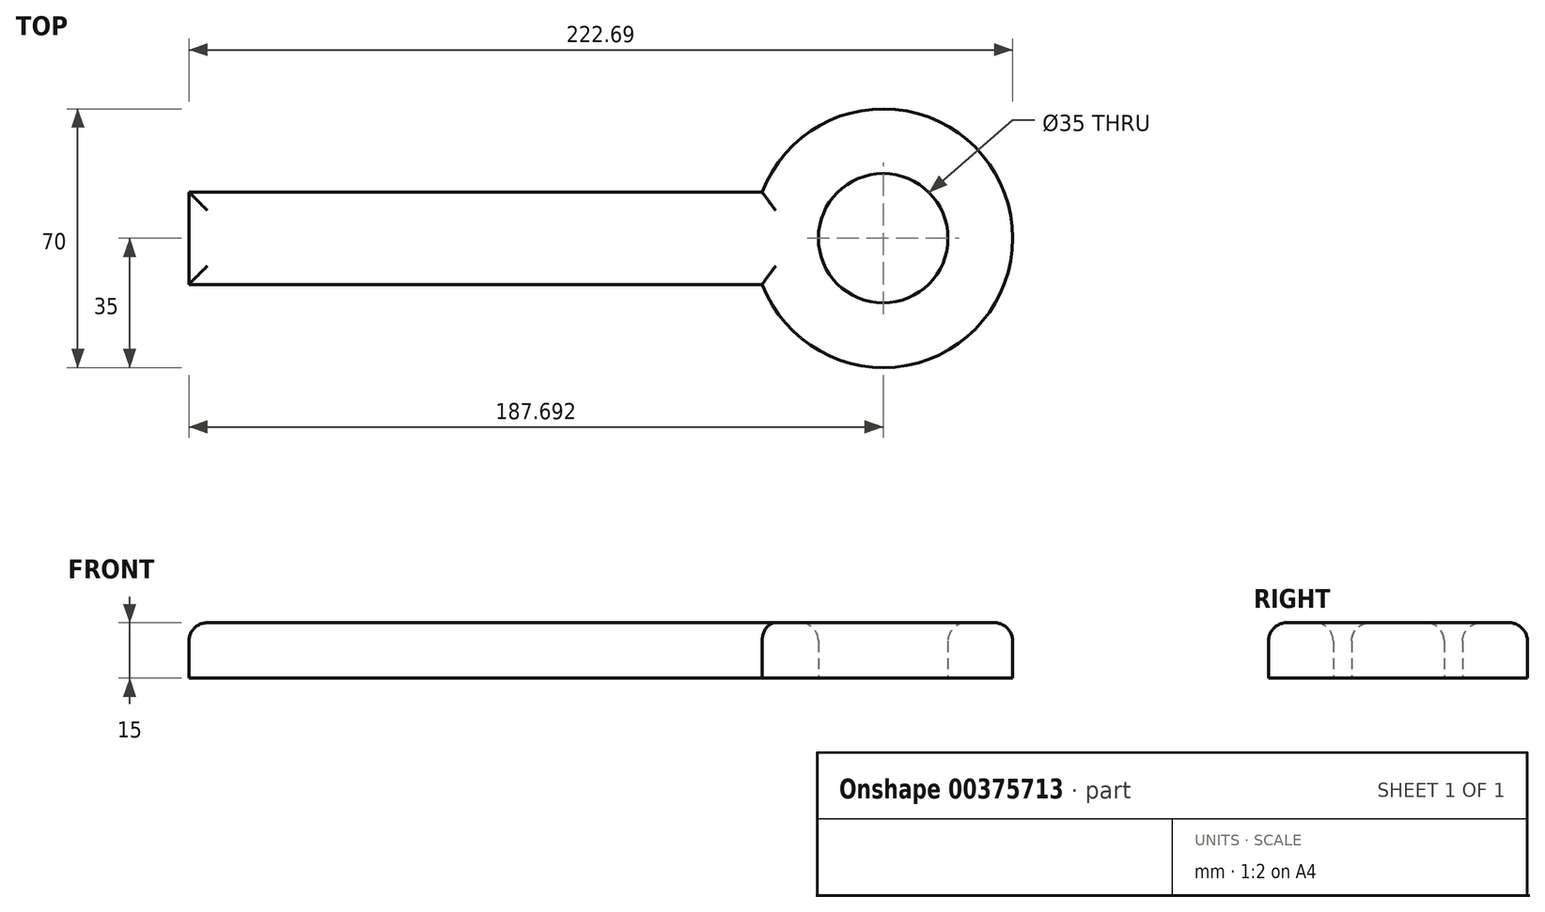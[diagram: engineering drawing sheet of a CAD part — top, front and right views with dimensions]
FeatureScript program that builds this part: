
annotation { "Feature Type Name" : "Feature", "Feature Type Description" : "" }
export const myFeature = defineFeature(function(context is Context, id is Id, definition is map)
    precondition{}
    {
        {
            var Q0;
            Q0=qCreatedBy(makeId("Top.planeOp"),FACE);
            var sketch = newSketch(context, id + "F0", { "sketchPlane" : qUnion([Q0])});
            skLineSegment(sketch, "E0.bottom", {"start": v(0, 0) * mm, "end": v(-155, 0) * mm});
            skLineSegment(sketch, "E0.top", {"start": v(0, 25) * mm, "end": v(-155, 25) * mm});
            skLineSegment(sketch, "E0.left", {"start": v(0, 0) * mm, "end": v(0, 25) * mm});
            skLineSegment(sketch, "E0.right", {"start": v(-155, 0) * mm, "end": v(-155, 25) * mm});
            skLineSegment(sketch, "E1.bottom", {"start": v(-155, 0) * mm, "end": v(-145, 0) * mm});
            skLineSegment(sketch, "E1.top", {"start": v(-155, -30) * mm, "end": v(-145, -30) * mm});
            skLineSegment(sketch, "E1.left", {"start": v(-155, 0) * mm, "end": v(-155, -30) * mm});
            skLineSegment(sketch, "E1.right", {"start": v(-145, 0) * mm, "end": v(-145, -30) * mm});
            skLineSegment(sketch, "E2.bottom", {"start": v(-130.68, 0) * mm, "end": v(-122.68, 0) * mm});
            skLineSegment(sketch, "E2.top", {"start": v(-130.68, -15) * mm, "end": v(-122.68, -15) * mm});
            skLineSegment(sketch, "E2.left", {"start": v(-130.68, 0) * mm, "end": v(-130.68, -15) * mm});
            skLineSegment(sketch, "E2.right", {"start": v(-122.68, 0) * mm, "end": v(-122.68, -15) * mm});
            skLineSegment(sketch, "E3", {"start": v(-94.28, 0) * mm, "end": v(-108.28, 0) * mm});
            skLineSegment(sketch, "E4", {"start": v(-94.28, 0) * mm, "end": v(-101.28, -15) * mm});
            skLineSegment(sketch, "E5", {"start": v(-108.28, 0) * mm, "end": v(-101.28, -15) * mm});
            skArc(sketch, "E6", {"start": v(0, 0) * mm, "mid": v(67.7, 12.5) * mm, "end": v(0, 25) * mm});
            skCircle(sketch, "E7", {"center": v(32.7, 12.5) * mm, "radius": 17.5 * mm});
            skLineSegment(sketch, "E8", {"start": v(32.7, 12.5) * mm, "end": v(-155, 12.5) * mm, "construction": true});
            skLineSegment(sketch, "E9", {"start": v(-101.28, -15) * mm, "end": v(-101.28, 0) * mm, "construction": true});
            skSolve(sketch);
        }
        {
            var Q0;
            Q0=makeQuery(id+"F0.imprint","IMPRINT",FACE,{"disambiguationData":[TD([[makeQuery(id+"F0.imprint","IMPRINT",EDGE,{"derivedFrom":sQuery(id+"F0.wireOp",EDGE,"E0.top")}),1.0]])]});
            var Q1;
            Q1=makeQuery(id+"F0.imprint","IMPRINT",FACE,{"disambiguationData":[TD([[makeQuery(id+"F0.imprint","IMPRINT",EDGE,{"derivedFrom":sQuery(id+"F0.wireOp",EDGE,"E0.left")}),-1.0]])]});
            var Q2;
            Q2=makeQuery(id+"F0.imprint","IMPRINT",FACE,{"disambiguationData":[TD([[makeQuery(id+"F0.imprint","IMPRINT",EDGE,{"derivedFrom":sQuery(id+"F0.wireOp",EDGE,"E1.bottom")}),-1.0]])]});
            var Q3;
            Q3=makeQuery(id+"F0.imprint","IMPRINT",FACE,{"disambiguationData":[TD([[makeQuery(id+"F0.imprint","IMPRINT",EDGE,{"derivedFrom":sQuery(id+"F0.wireOp",EDGE,"E2.bottom")}),-1.0]])]});
            var Q4;
            Q4=makeQuery(id+"F0.imprint","IMPRINT",FACE,{"disambiguationData":[TD([[makeQuery(id+"F0.imprint","IMPRINT",EDGE,{"derivedFrom":sQuery(id+"F0.wireOp",EDGE,"E3")}),1.0]])]});
            extrude(context, id + "F1", {"entities" : qUnion([Q0, Q1, Q2, Q3, Q4]), "depth" : 15 * mm});
        }
        {
            var Q0;
            Q0=makeQuery(id+"F1.opExtrude","CAP_EDGE",EDGE,{"disambiguationData":[OSD([sQuery(id+"F0.wireOp",EDGE,"E0.top")])],"isStart":false});
            var Q1;
            Q1=makeQuery(id+"F1.opExtrude","CAP_EDGE",EDGE,{"disambiguationData":[OSD([sQuery(id+"F0.wireOp",EDGE,"E0.right"),sQuery(id+"F0.wireOp",EDGE,"E1.left")])],"isStart":false});
            var Q2;
            Q2=makeQuery(id+"F1.opExtrude","CAP_FACE",FACE,{"disambiguationData":[OSD([sQuery(id+"F0.wireOp",EDGE,"E0.bottom"),sQuery(id+"F0.wireOp",EDGE,"E0.top"),sQuery(id+"F0.wireOp",EDGE,"E0.right"),sQuery(id+"F0.wireOp",EDGE,"E1.top"),sQuery(id+"F0.wireOp",EDGE,"E1.left"),sQuery(id+"F0.wireOp",EDGE,"E1.right"),sQuery(id+"F0.wireOp",EDGE,"E2.top"),sQuery(id+"F0.wireOp",EDGE,"E2.left"),sQuery(id+"F0.wireOp",EDGE,"E2.right"),sQuery(id+"F0.wireOp",EDGE,"E4"),sQuery(id+"F0.wireOp",EDGE,"E5"),sQuery(id+"F0.wireOp",EDGE,"E6"),sQuery(id+"F0.wireOp",EDGE,"E7")])],"isStart":false});
            var Q3;
            Q3=makeQuery(id+"F1.opExtrude","CAP_EDGE",EDGE,{"disambiguationData":[OSD([sQuery(id+"F0.wireOp",EDGE,"E1.right")])],"isStart":false});
            var Q4;
            Q4=makeQuery(id+"F1.opExtrude","CAP_EDGE",EDGE,{"disambiguationData":[OSD([sQuery(id+"F0.wireOp",EDGE,"E2.left")])],"isStart":false});
            var Q5;
            {var subQ0=sQuery(id+"F0.wireOp",EDGE,"E0.bottom");Q5=makeQuery(id+"F1.opExtrude","CAP_EDGE",EDGE,{"disambiguationData":[OSD([subQ0]),TDD([makeQuery(id+"F0.imprint","IMPRINT",EDGE,{"disambiguationData":[TD([[makeQuery(id+"F0.imprint","INTERSECT",VERTEX,{"derivedFrom":[subQ0,sQuery(id+"F0.wireOp",EDGE,"E1.bottom"),sQuery(id+"F0.wireOp",EDGE,"E1.right")]}),1.0]])],"derivedFrom":subQ0})])],"isStart":false});}
            var Q6;
            Q6=makeQuery(id+"F1.opExtrude","CAP_EDGE",EDGE,{"disambiguationData":[OSD([sQuery(id+"F0.wireOp",EDGE,"E2.right")])],"isStart":false});
            var Q7;
            Q7=makeQuery(id+"F1.opExtrude","CAP_EDGE",EDGE,{"disambiguationData":[OSD([sQuery(id+"F0.wireOp",EDGE,"E2.top")])],"isStart":false});
            var Q8;
            Q8=makeQuery(id+"F1.opExtrude","CAP_EDGE",EDGE,{"disambiguationData":[OSD([sQuery(id+"F0.wireOp",EDGE,"E5")])],"isStart":false});
            var Q9;
            {var subQ0=sQuery(id+"F0.wireOp",EDGE,"E0.bottom");Q9=makeQuery(id+"F1.opExtrude","CAP_EDGE",EDGE,{"disambiguationData":[OSD([subQ0]),TDD([makeQuery(id+"F0.imprint","IMPRINT",EDGE,{"disambiguationData":[TD([[makeQuery(id+"F0.imprint","INTERSECT",VERTEX,{"derivedFrom":[subQ0,sQuery(id+"F0.wireOp",EDGE,"E2.bottom"),sQuery(id+"F0.wireOp",EDGE,"E2.right")]}),1.0]])],"derivedFrom":subQ0})])],"isStart":false});}
            var Q10;
            Q10=makeQuery(id+"F1.opExtrude","CAP_EDGE",EDGE,{"disambiguationData":[OSD([sQuery(id+"F0.wireOp",EDGE,"E4")])],"isStart":false});
            var Q11;
            {var subQ0=sQuery(id+"F0.wireOp",EDGE,"E0.bottom");Q11=makeQuery(id+"F1.opExtrude","CAP_EDGE",EDGE,{"disambiguationData":[OSD([subQ0]),TDD([makeQuery(id+"F0.imprint","IMPRINT",EDGE,{"disambiguationData":[TD([[makeQuery(id+"F0.imprint","INTERSECT",VERTEX,{"derivedFrom":[subQ0,sQuery(id+"F0.wireOp",EDGE,"E0.left"),sQuery(id+"F0.wireOp",EDGE,"E6")]}),-1.0]])],"derivedFrom":subQ0})])],"isStart":false});}
            var Q12;
            Q12=makeQuery(id+"F1.opExtrude","CAP_EDGE",EDGE,{"disambiguationData":[OSD([sQuery(id+"F0.wireOp",EDGE,"E6")])],"isStart":false});
            var Q13;
            Q13=makeQuery(id+"F1.opExtrude","CAP_EDGE",EDGE,{"disambiguationData":[OSD([sQuery(id+"F0.wireOp",EDGE,"E7")])],"isStart":false});
            fillet(context, id + "F2", {"entities" : qUnion([Q0, Q1, Q2, Q3, Q4, Q5, Q6, Q7, Q8, Q9, Q10, Q11, Q12, Q13]), "radius" : 5 * mm, "tangentPropagation" : true, "allowEdgeOverflow" : false});
        }
    });
